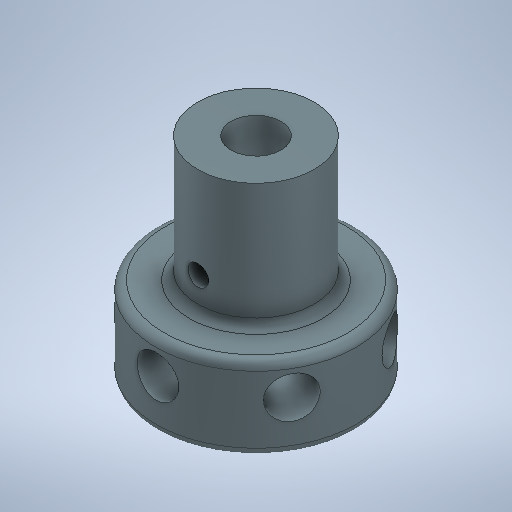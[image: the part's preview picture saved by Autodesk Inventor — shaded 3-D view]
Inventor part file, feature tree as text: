
AUTODESK INVENTOR PART (.ipt)
format: ipt  version: 2025.1 (Build 291241000, 241)  size: 356,864 bytes
history: native  units: mm
features: sketch x5, hole x3, extrude x2, plane x2, fillet x1, pattern_circular x1, projected_geometry x1
ambient origin geometry x8: Origin, YZ Plane, XZ Plane, XY Plane, X Axis, Y Axis, Z Axis, Center Point
bodies: Solid1 (feature_tree)
feature tree (15):
  extrude  "Extrusion1"  Depth=10.0mm TaperAngle=0.0deg
  extrude  "Extrusion2"  Depth=15.0mm TaperAngle=0.0deg
  fillet  "Fillet1"  Radius=1.0mm
  plane  "Work Plane1"
  hole  "Hole2"  [1 undecoded]
  pattern_circular  "Circular Pattern1"  Count=6 Angle=360.0deg
  plane  "Work Plane2"
  hole  "Hole3"  [1 undecoded]
  hole  "Hole4"  [1 undecoded]
  sketch  "Sketch1"  dims[d0=24.0mm d1=10.0mm d2=0.0mm]
  sketch  "Sketch2"  dims[d3=14.0mm d4=15.0mm d5=0.0mm d13=1.0mm]
  sketch  "Sketch4"  dims[d14=12.0mm d15=6.0mm]
  sketch  "Sketch5"  dims[d16=5.0mm d17=6.0mm d18=4.0mm d19=2.0mm d20=90.0deg d21=8.0mm d22=0.0mm d23=60.0mm d24=360.0deg]
  projected_geometry  "Projected Loop1"
  sketch  "Sketch6"  dims[d26=7.0mm d27=11.0mm d28=2.459mm d29=6.0mm d30=4.0mm d31=2.0mm d32=90.0deg d33=8.8mm d34=0.0mm d35=6.0mm d36=6.0mm d37=4.0mm d38=2.0mm d39=90.0deg d40=8.0mm d41=0.0mm]
note: 3 required parameter values undecoded (feature->parameter linkage not recoverable at this tier; creation-order binding heuristic only, values carry confidence <= 0.55)
